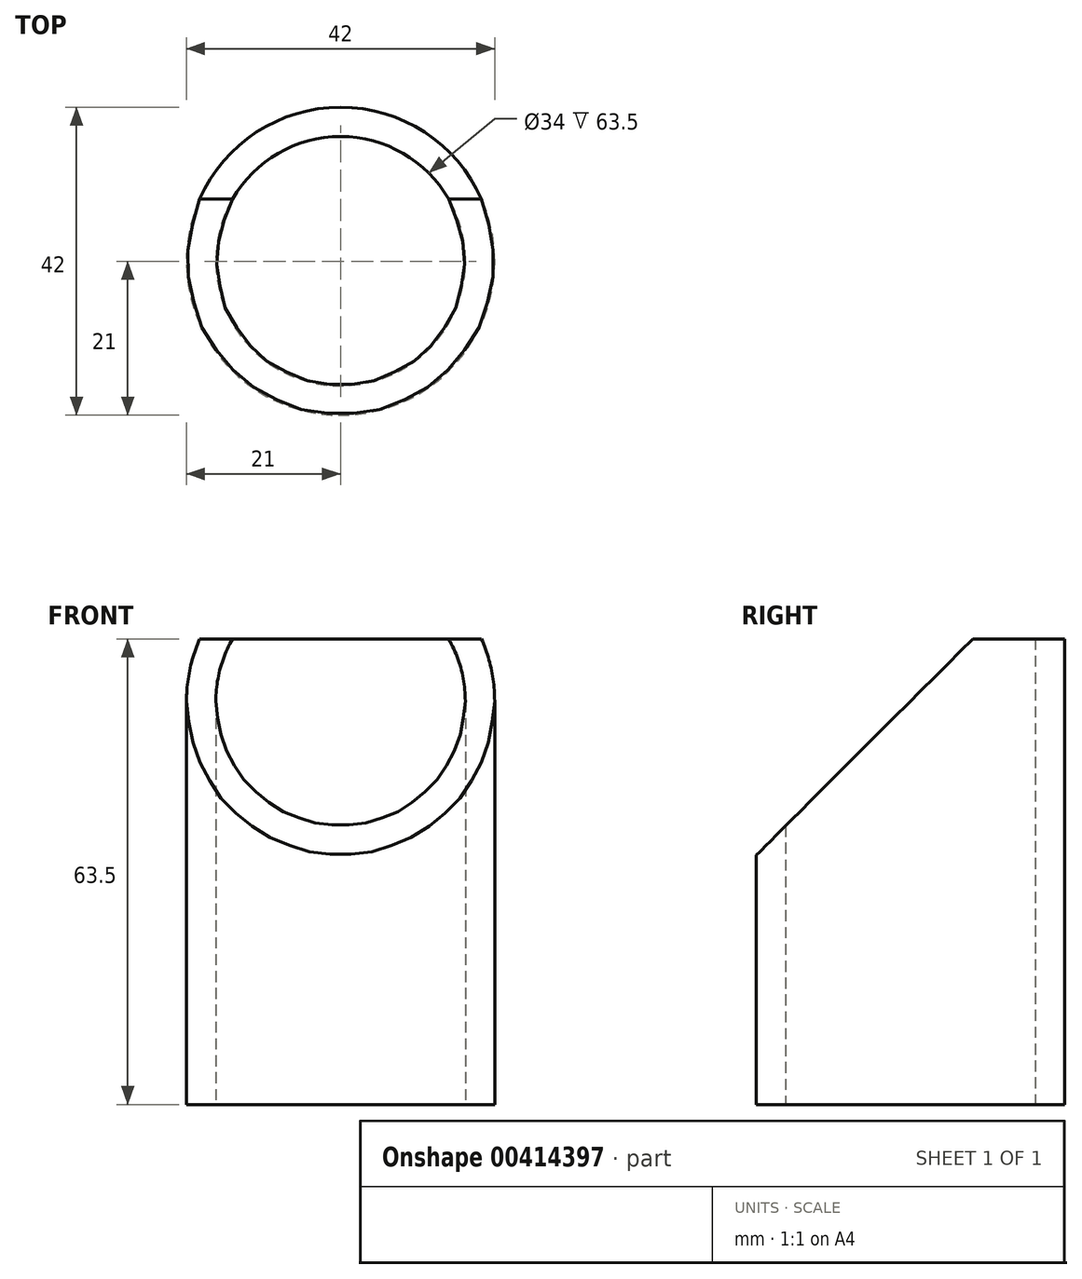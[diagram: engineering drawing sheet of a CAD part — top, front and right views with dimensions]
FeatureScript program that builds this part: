
annotation { "Feature Type Name" : "Feature", "Feature Type Description" : "" }
export const myFeature = defineFeature(function(context is Context, id is Id, definition is map)
    precondition{}
    {
        {
            var Q0;
            Q0=qCreatedBy(makeId("Top.planeOp"),FACE);
            var sketch = newSketch(context, id + "F0", { "sketchPlane" : qUnion([Q0])});
            skCircle(sketch, "E0", {"center": v(0, 0) * mm, "radius": 17 * mm});
            skCircle(sketch, "E1.0", {"center": v(0, 0) * mm, "radius": 21 * mm});
            skSolve(sketch);
        }
        {
            var Q0;
            Q0=qSketchRegion(id+"F0",true);
            var Q1;
            Q1 = qSketchRegion(id + "F2", true);
            extrude(context, id + "F1", {"entities" : qUnion([Q0, Q1]), "offsetDistance" : 25.4 * mm, "depth" : 63.5 * mm});
        }
        {
            var Q0;
            Q0=qCreatedBy(makeId("Right.planeOp"),FACE);
            var sketch = newSketch(context, id + "F2", { "sketchPlane" : qUnion([Q0])});
            skLineSegment(sketch, "E2", {"start": v(8.5, 63.5) * mm, "end": v(-21, 34) * mm});
            skLineSegment(sketch, "E3", {"start": v(8.5, 63.5) * mm, "end": v(21, 63.5) * mm});
            skLineSegment(sketch, "E4", {"start": v(-21, 34) * mm, "end": v(-21, 73.5) * mm});
            skLineSegment(sketch, "E5", {"start": v(-21, 73.5) * mm, "end": v(21, 73.5) * mm});
            skLineSegment(sketch, "E6", {"start": v(21, 73.5) * mm, "end": v(21, 63.5) * mm});
            skPoint(sketch, "E7", {"position": v(0, 73.5) * mm});
            skLineSegment(sketch, "E8.MirrorCS", {"start": v(8.5, -63.5) * mm, "end": v(21, -63.5) * mm});
            skLineSegment(sketch, "E9.MirrorCS", {"start": v(-21, -73.5) * mm, "end": v(21, -73.5) * mm});
            skLineSegment(sketch, "E10.MirrorCS", {"start": v(8.5, -63.5) * mm, "end": v(-21, -34) * mm});
            skLineSegment(sketch, "E11.MirrorCS", {"start": v(21, -73.5) * mm, "end": v(21, -63.5) * mm});
            skLineSegment(sketch, "E12.MirrorCS", {"start": v(-21, -34) * mm, "end": v(-21, -73.5) * mm});
            skPoint(sketch, "E13.MirrorP", {"position": v(0, -73.5) * mm});
            skSolve(sketch);
        }
        {
            var Q0;
            Q0=qSketchRegion(id+"F2",true);
            extrude(context, id + "F3", {"entities" : qUnion([Q0]), "operationType" : NewBodyOperationType.REMOVE, "endBound" : BoundingType.SYMMETRIC, "oppositeDirection" : true, "depth" : 42 * mm});
        }
    });
